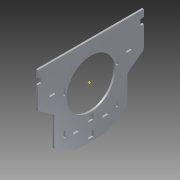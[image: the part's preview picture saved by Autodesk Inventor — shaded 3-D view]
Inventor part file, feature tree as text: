
AUTODESK INVENTOR PART (.ipt)
format: ipt  version: 2013 (Build 170138000, 138)  size: 238,592 bytes
history: native  units: mm
features: extrude x1, sketch x1
ambient origin geometry x8: Origin, YZ Plane, XZ Plane, XY Plane, X Axis, Y Axis, Z Axis, Center Point
feature tree (2):
  extrude  "Extrusion6"  Depth=6.0mm
  sketch  "Sketch2"  dims[d8=0.0mm d21=6.0mm d22=10.0mm d25=6.0mm d26=10.0mm d31=3.0mm d32=10.0mm d35=3.0mm d36=10.0mm d39=25.0mm d40=25.0mm d43=82.55mm d52=3.0mm d53=10.0mm d54=10.0mm d55=3.0mm d58=10.0mm d59=3.0mm d62=3.0mm d65=180.0mm d69=20.0mm d71=20.0mm d72=43.5mm d73=43.5mm d74=60.0mm d75=60.0mm d76=10.0mm d77=10.0mm d78=60.0mm d79=90.0mm d80=43.5mm d81=43.5mm d87=15.0mm d90=90.0mm d91=90.0mm d103=10.0mm d104=10.0mm d108=3.0mm d109=10.0mm d110=20.0mm d111=3.0mm d112=10.0mm d113=20.0mm d114=5.0mm d115=10.0mm d116=9.0mm d117=4.5mm d118=10.0mm d119=9.0mm d120=15.0mm d121=4.5mm d124=3.0mm d125=0.0mm d127=180.0mm d128=150.0mm d130=85.5mm d131=43.5mm d132=43.5mm d133=60.0mm d134=60.0mm d135=43.5mm d136=43.5mm d137=90.0deg d138=28.0mm d140=47.0mm d141=47.0mm d144=60.0mm d145=20.0mm d147=65.0mm d149=50.0mm d151=10.0mm d152=60.0mm d153=20.0mm d154=50.0mm d155=62.0mm d156=62.0mm d157=62.0mm d158=57.0mm d159=57.0mm d160=3.0mm d161=24.0mm d162=24.0mm d163=90.0mm d164=5.0mm]
